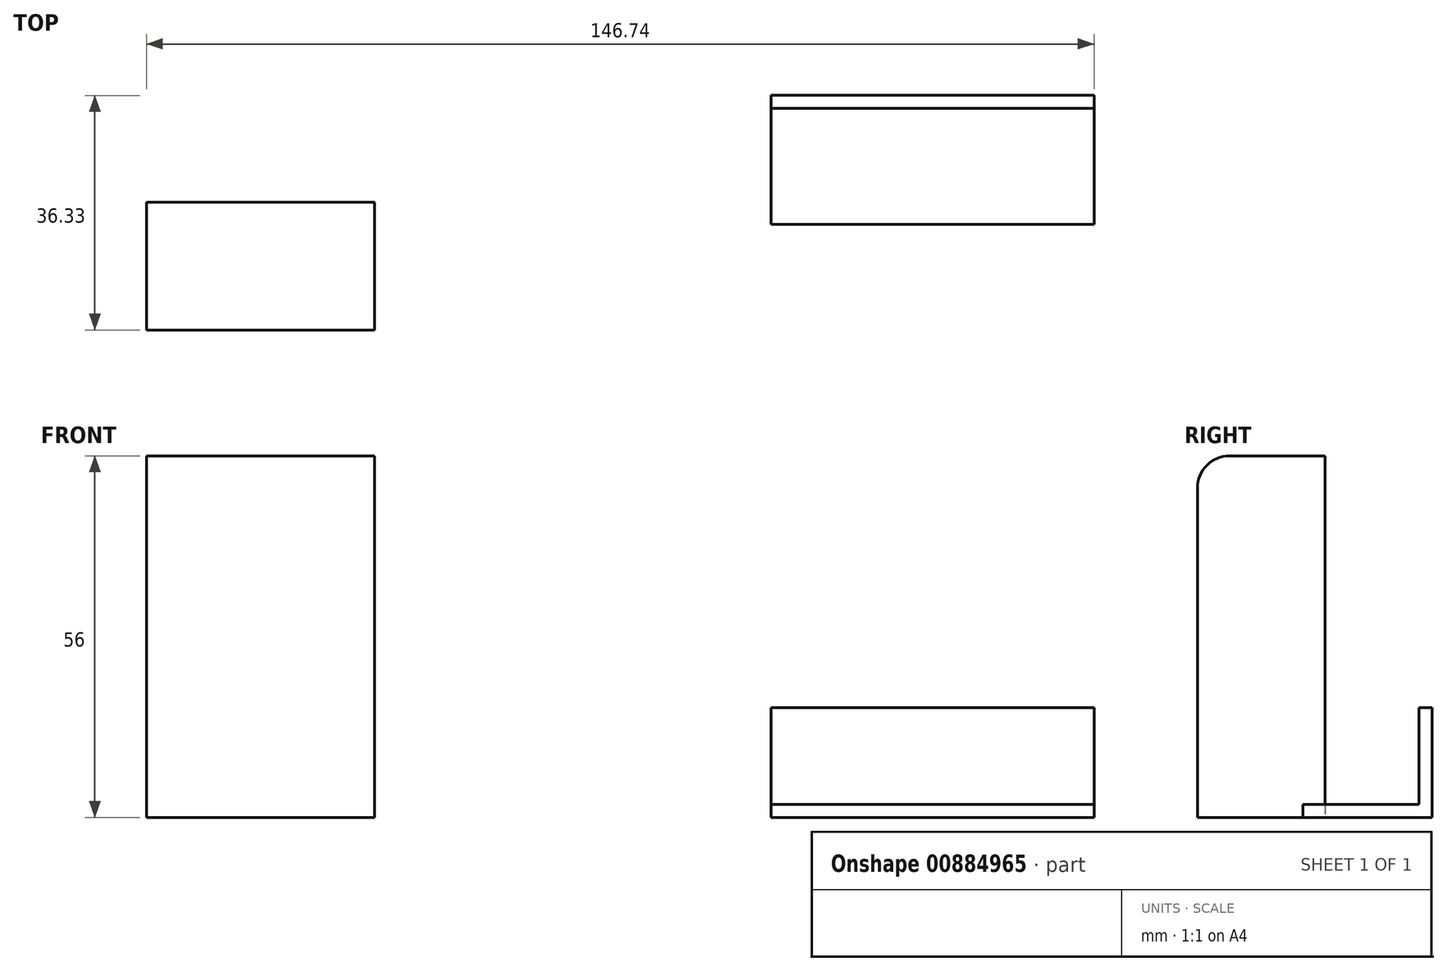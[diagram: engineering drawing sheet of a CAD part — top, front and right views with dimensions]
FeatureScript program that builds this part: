
annotation { "Feature Type Name" : "Feature", "Feature Type Description" : "" }
export const myFeature = defineFeature(function(context is Context, id is Id, definition is map)
    precondition{}
    {
        {
            var Q0;
            Q0=qCreatedBy(makeId("Top.planeOp"),FACE);
            var sketch = newSketch(context, id + "F0", { "sketchPlane" : qUnion([Q0])});
            skLineSegment(sketch, "E0.bottom", {"start": v(-52.45, 31.86) * mm, "end": v(-17.11, 31.86) * mm});
            skLineSegment(sketch, "E0.top", {"start": v(-52.45, 12.1) * mm, "end": v(-17.11, 12.1) * mm});
            skLineSegment(sketch, "E0.left", {"start": v(-52.45, 31.86) * mm, "end": v(-52.45, 12.1) * mm});
            skLineSegment(sketch, "E0.right", {"start": v(-17.11, 31.86) * mm, "end": v(-17.11, 12.1) * mm});
            skSolve(sketch);
        }
        {
            var Q0;
            Q0 = qSketchRegion(id + "F0", true);
            extrude(context, id + "F1", {"entities" : qUnion([Q0]), "depth" : 56 * mm, "offsetDistance" : 25 * mm});
        }
        {
            var Q0;
            Q0=makeQuery(id+"F1.opExtrude","CAP_EDGE",EDGE,{"disambiguationData":[OSD([sQuery(id+"F0.wireOp",EDGE,"E0.top")])],"isStart":false});
            fillet(context, id + "F2", {"entities" : qUnion([Q0]), "radius" : 5 * mm, "tangentPropagation" : true, "allowEdgeOverflow" : false});
        }
        {
            var Q0;
            Q0=qCreatedBy(makeId("Top.planeOp"),FACE);
            var sketch = newSketch(context, id + "F3", { "sketchPlane" : qUnion([Q0])});
            skLineSegment(sketch, "E1.bottom", {"start": v(44.3, 48.43) * mm, "end": v(94.3, 48.43) * mm});
            skLineSegment(sketch, "E1.top", {"start": v(44.3, 28.43) * mm, "end": v(94.3, 28.43) * mm});
            skLineSegment(sketch, "E1.left", {"start": v(44.3, 48.43) * mm, "end": v(44.3, 28.43) * mm});
            skLineSegment(sketch, "E1.right", {"start": v(94.3, 48.43) * mm, "end": v(94.3, 28.43) * mm});
            skSolve(sketch);
        }
        {
            var Q0;
            Q0=makeQuery(id+"F3.imprint","IMPRINT",FACE,{"disambiguationData":[TD([[makeQuery(id+"F3.imprint","IMPRINT",EDGE,{"derivedFrom":sQuery(id+"F3.wireOp",EDGE,"E1.bottom")}),-1.0]])]});
            extrude(context, id + "F4", {"entities" : qUnion([Q0]), "depth" : 2 * mm, "offsetDistance" : 25 * mm});
        }
        {
            var Q0;
            Q0=makeQuery(id+"F4.opExtrude","CAP_FACE",FACE,{"disambiguationData":[OSD([sQuery(id+"F3.wireOp",EDGE,"E1.bottom"),sQuery(id+"F3.wireOp",EDGE,"E1.top"),sQuery(id+"F3.wireOp",EDGE,"E1.left"),sQuery(id+"F3.wireOp",EDGE,"E1.right")])],"isStart":false});
            var sketch = newSketch(context, id + "F5", { "sketchPlane" : qUnion([Q0])});
            skLineSegment(sketch, "E2.bottom", {"start": v(44.3, 48.43) * mm, "end": v(94.3, 48.43) * mm});
            skLineSegment(sketch, "E2.top", {"start": v(44.3, 46.43) * mm, "end": v(94.3, 46.43) * mm});
            skLineSegment(sketch, "E2.left", {"start": v(44.3, 48.43) * mm, "end": v(44.3, 46.43) * mm});
            skLineSegment(sketch, "E2.right", {"start": v(94.3, 48.43) * mm, "end": v(94.3, 46.43) * mm});
            skSolve(sketch);
        }
        {
            var Q0;
            Q0=makeQuery(id+"F5.imprint","IMPRINT",FACE,{"disambiguationData":[TD([[makeQuery(id+"F5.imprint","IMPRINT",EDGE,{"derivedFrom":sQuery(id+"F5.wireOp",EDGE,"E2.bottom")}),-1.0]])]});
            extrude(context, id + "F6", {"entities" : qUnion([Q0]), "operationType" : NewBodyOperationType.ADD, "depth" : 15 * mm, "offsetDistance" : 25 * mm});
        }
    });
